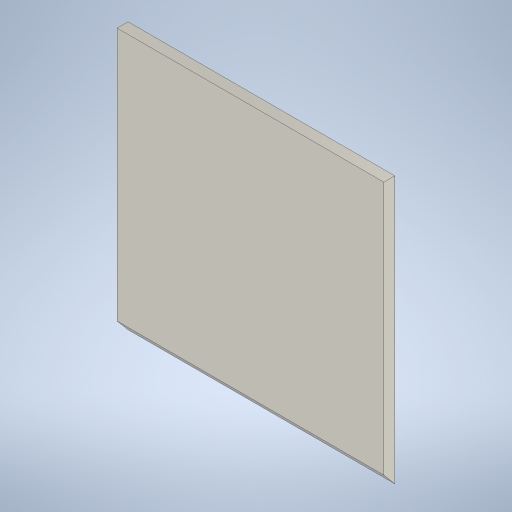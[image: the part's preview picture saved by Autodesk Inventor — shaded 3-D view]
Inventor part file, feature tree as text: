
AUTODESK INVENTOR PART (.ipt)
format: ipt  version: 2023 (Build 270158000, 158)  size: 211,968 bytes
history: native  units: in
note: dims shown in document units (in); Inventor stores cm internally (conversion verified against a paired STEP export)
features: extrude x2, sketch x2, projected_geometry x1
ambient origin geometry x8: Origin, YZ Plane, XZ Plane, XY Plane, X Axis, Y Axis, Z Axis, Center Point
bodies: Solid1 (feature_tree)
feature tree (5):
  extrude  "Extrusion1"  Depth=3.8189in
  extrude  "Extrusion2"  Depth=0.1575in
  sketch  "Sketch1"  dims[d0=3.8189in d1=3.8189in]
  sketch  "Sketch3"  dims[d2=0.1575in d3=0.0in d11=0.2756in d12=0.2749in d13=0.0in d14=0.0in]
  projected_geometry  "Projected Loop1"
